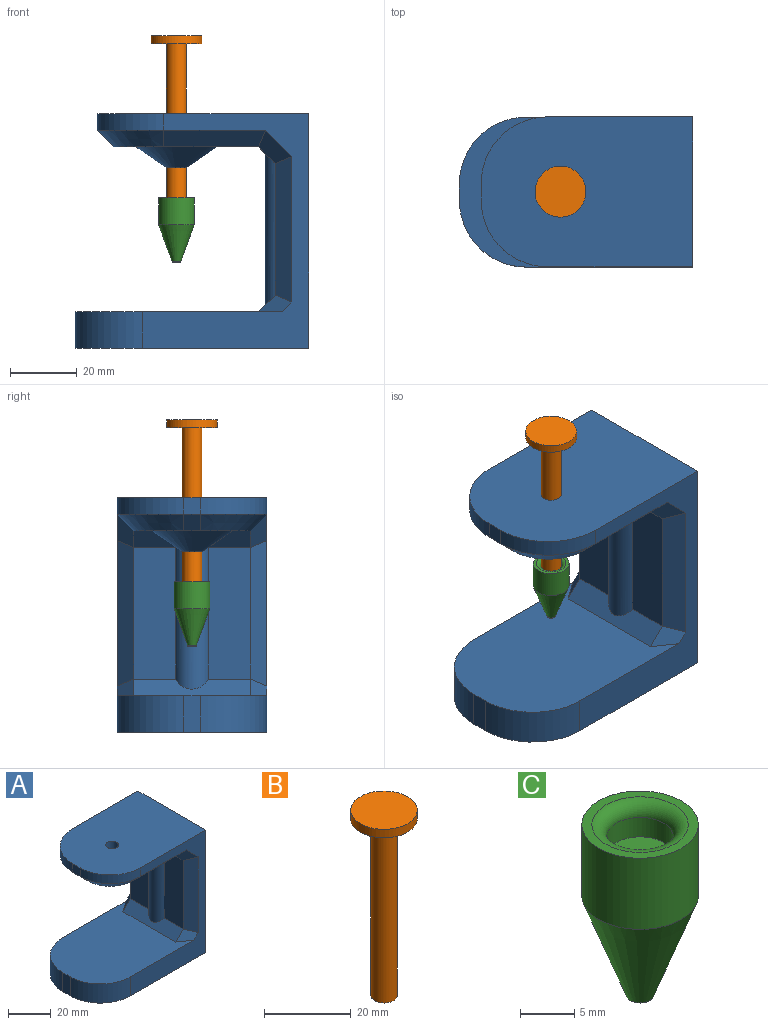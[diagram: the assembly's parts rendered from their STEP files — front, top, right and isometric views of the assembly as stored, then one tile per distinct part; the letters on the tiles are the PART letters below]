
ASSEMBLY  parts=3 mates=2
PART A: 33 faces, bbox 70x45x70.5 mm
  f0: plane 6.11x6.11mm, normal (0,0,-1), area 1.1mm2, adj f18,f31
  f1: plane 39.51x12.64mm, normal (-1,0,0), area 499.4mm2, adj f12,f13,f28,f30
  f2: plane 70.47x45mm, normal (1,0,0), area 3171.1mm2, adj f3,f9,f10,f11
  f3: plane 63.49x45mm, normal (0,0,1), area 2657.1mm2, adj f2,f4,f10,f11,f15,f17,f18
  f4: plane 5x5mm, normal (-1,0,0), area 25mm2, adj f3,f15,f17,f24
  f5: plane 43.49x35mm, normal (0,0,-1), area 961.3mm2, adj f13,f22,f23,f24,f25,f26,f32
  f6: plane 39.51x12.64mm, normal (-1,0,0), area 499.4mm2, adj f12,f13,f20,f30
  f7: plane 62.07x45mm, normal (0,0,1), area 2338.7mm2, adj f8,f10,f11,f12,f14,f16,f19,f29
  f8: plane 10.96x5mm, normal (-1,0,0), area 54.8mm2, adj f7,f9,f14,f16
  f9: plane 70x45mm, normal (0,0,-1), area 2978.3mm2, adj f2,f8,f10,f11,f14,f16
  f10: plane 70.47x50mm, normal (0,-1,0), area 1073.8mm2, adj f2,f3,f7,f9,f16,f17,f26,f27
  f11: plane 70.47x50mm, normal (0,1,0), area 1073.8mm2, adj f2,f3,f7,f9,f14,f15,f19,f20
  f12: plane 35x5mm, normal (-0.71,0,0.71), area 217.7mm2, adj f1,f6,f7,f19,f29,f30
  f13: plane 35x5mm, normal (-0.71,0,-0.71), area 217.7mm2, adj f1,f5,f6,f21,f27,f30
  f14: cylinder r=20mm len=20mm, axis (0,0,-1), area 344.4mm2, adj f7,f8,f9,f11
  f15: cylinder r=20mm len=20mm, axis (0,0,-1), area 157.1mm2, adj f3,f4,f11,f23
  f16: cylinder r=20mm len=20mm, axis (0,0,1), area 344.4mm2, adj f7,f8,f9,f10
  f17: cylinder r=20mm len=20mm, axis (0,0,1), area 157.1mm2, adj f3,f4,f10,f25
  f18: cylinder r=3mm len=10mm, axis (0,0,-1), area 188.5mm2, adj f0,f3
  f19: plane 10x5mm, normal (-0.5,0.71,0.5), area 39.6mm2, adj f7,f11,f12,f20
  f20: plane 43.65x5mm, normal (-0.71,0.71,0), area 294mm2, adj f6,f11,f19,f21
  f21: plane 10x10mm, normal (-0.5,0.71,-0.5), area 64.6mm2, adj f11,f13,f20,f22
  f22: plane 30.56x5mm, normal (0,0.71,-0.71), area 208.8mm2, adj f5,f11,f21,f23
  f23: cone r=15mm half-angle=45deg, axis (0,0,1), area 194.4mm2, adj f5,f15,f22,f24
  f24: plane 5x5mm, normal (-0.71,0,-0.71), area 35.4mm2, adj f4,f5,f23,f25
  f25: cone r=15mm half-angle=45deg, axis (0,0,1), area 194.4mm2, adj f5,f17,f24,f26
  f26: plane 30.56x5mm, normal (0,-0.71,-0.71), area 208.8mm2, adj f5,f10,f25,f27
  f27: plane 10x10mm, normal (-0.5,-0.71,-0.5), area 64.6mm2, adj f10,f13,f26,f28
  f28: plane 43.65x5mm, normal (-0.71,-0.71,0), area 294mm2, adj f1,f10,f27,f29
  f29: plane 10x5mm, normal (-0.5,-0.71,0.5), area 39.6mm2, adj f7,f10,f12,f28
  f30: cylinder r=5.42mm len=45.57mm, axis (0,0,1), area 524.1mm2, adj f1,f6,f12,f13
  f31: cylinder r=3.06mm len=6.26mm, axis (0,0,1), area 120.2mm2, adj f0,f32
  f32: cone r=3.06mm half-angle=55.5deg, axis (0,0,1), area 527.8mm2, adj f5,f31
PART B: 5 faces, bbox 15.3x15.3x52.2 mm
  f0: plane 15.3x15.3mm, normal (0,0,1), area 183.8mm2, adj f1
  f1: cylinder r=7.65mm len=15.3mm, axis (0,0,1), area 115mm2, adj f0,f2
  f2: plane 15.3x15.3mm, normal (0,0,-1), area 155.5mm2, adj f1,f3
  f3: cylinder r=3mm len=49.82mm, axis (0,0,1), area 939.4mm2, adj f2,f4
  f4: plane 6x6mm, normal (0,0,-1), area 28.3mm2, adj f3
PART C: 8 faces, bbox 10.8x10.8x19.4 mm
  f0: plane 6.17x6.17mm, normal (0,0,1), area 26.8mm2, adj f1,f7
  f1: cylinder r=3.08mm len=6.17mm, axis (0,0,1), area 42.6mm2, adj f0,f2
  f2: torus R=4.45mm, axis (0,0,1), area 48.4mm2, adj f1,f3
  f3: plane 10.77x10.77mm, normal (0,0,1), area 28.7mm2, adj f2,f4
  f4: cylinder r=5.38mm len=10.77mm, axis (0,0,1), area 272.2mm2, adj f3,f5
  f5: cone r=5.38mm half-angle=20.2deg, axis (0,0,1), area 249.2mm2, adj f4,f6
  f6: torus R=1.12mm, axis (0,0,1), area 2.6mm2, adj f5,f7
  f7: cylinder r=0.99mm len=15.66mm, axis (0,0,1), area 97mm2, adj f0,f6
PLACE A t=(0,0,-9.96)mm fixed
PLACE B rot(axis=(0,0,-1),164.2deg) t=(34.02,4.72,1.74)mm
PLACE C rot(axis=(0,0,-1),74.2deg) t=(12.62,16.68,1.93)mm
MATE fastened B.f1 <-> C.f1  axis (0,0,-1) through (17.34,0,-43.08)mm
MATE cylindrical A.f18 <-> B.f1  axis (0,0,1) through (17.34,0,-14.21)mm
